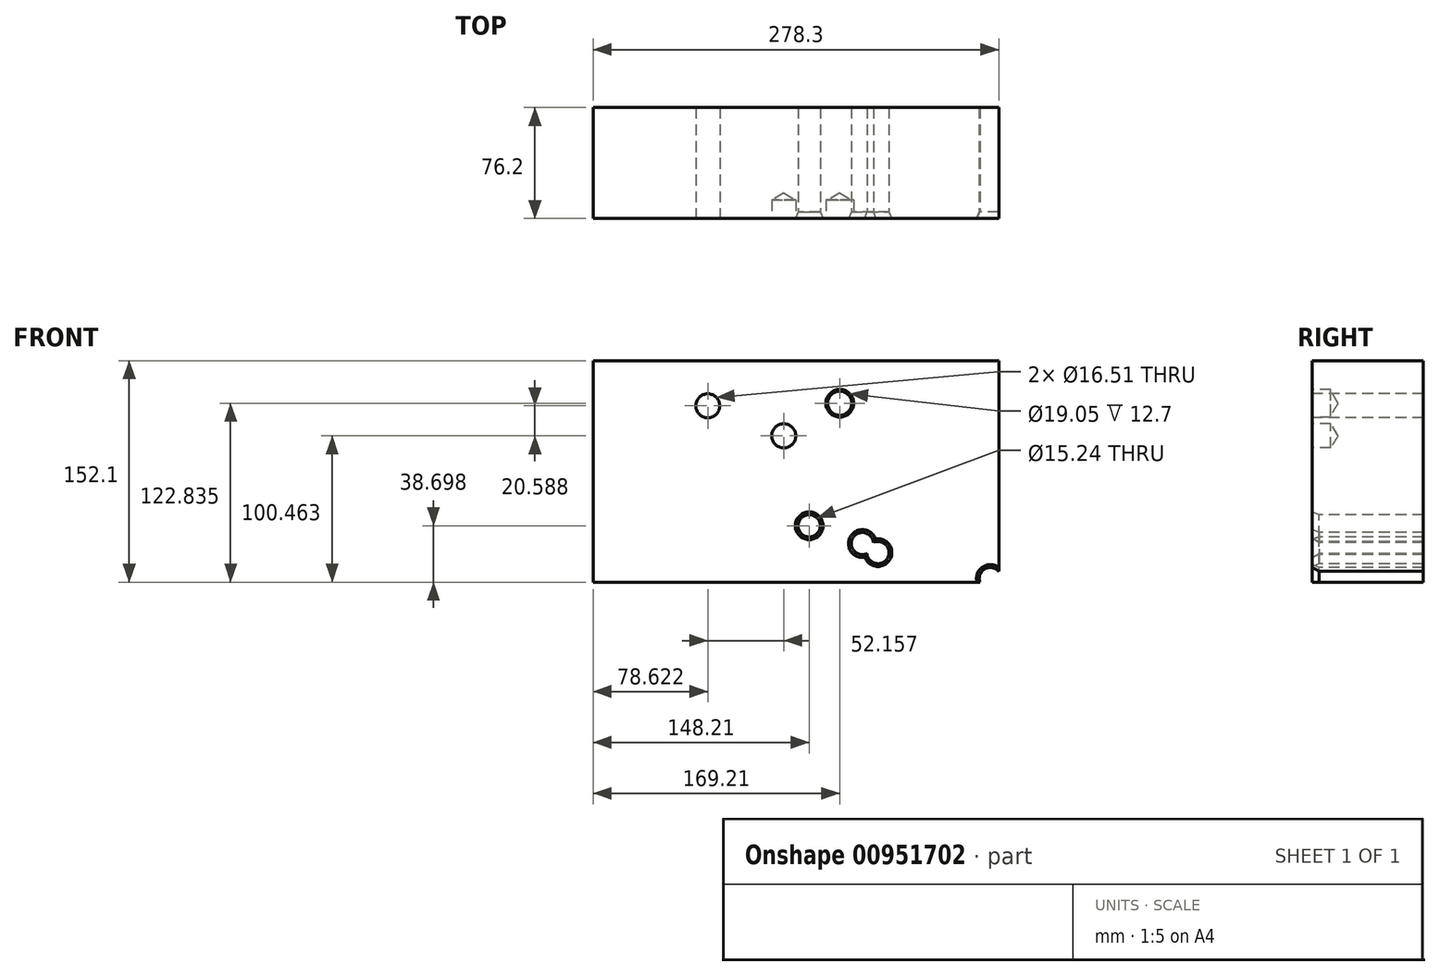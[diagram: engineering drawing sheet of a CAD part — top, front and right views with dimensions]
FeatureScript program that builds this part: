
annotation { "Feature Type Name" : "Feature", "Feature Type Description" : "" }
export const myFeature = defineFeature(function(context is Context, id is Id, definition is map)
    precondition{}
    {
        {
            var Q0;
            Q0=qCreatedBy(makeId("Front.planeOp"),FACE);
            var sketch = newSketch(context, id + "F0", { "sketchPlane" : qUnion([Q0])});
            skLineSegment(sketch, "E0.bottom", {"start": v(-137.1, 77.72) * mm, "end": v(141.2, 77.72) * mm});
            skLineSegment(sketch, "E0.top", {"start": v(-137.1, -74.38) * mm, "end": v(141.2, -74.38) * mm});
            skLineSegment(sketch, "E0.left", {"start": v(-137.1, 77.72) * mm, "end": v(-137.1, -74.38) * mm});
            skLineSegment(sketch, "E0.right", {"start": v(141.2, 77.72) * mm, "end": v(141.2, -74.38) * mm});
            skSolve(sketch);
        }
        {
            var Q0;
            Q0=makeQuery(id+"F0.imprint","IMPRINT",FACE,{"disambiguationData":[TD([[makeQuery(id+"F0.imprint","IMPRINT",EDGE,{"derivedFrom":sQuery(id+"F0.wireOp",EDGE,"E0.bottom")}),-1.0]])]});
            extrude(context, id + "F1", {"entities" : qUnion([Q0]), "depth" : 76.2 * mm, "offsetDistance" : 25.4 * mm});
        }
        {
            var Q0;
            Q0=makeQuery(id+"F1.opExtrude","CAP_FACE",FACE,{"disambiguationData":[OSD([sQuery(id+"F0.wireOp",EDGE,"E0.bottom"),sQuery(id+"F0.wireOp",EDGE,"E0.top"),sQuery(id+"F0.wireOp",EDGE,"E0.left"),sQuery(id+"F0.wireOp",EDGE,"E0.right")])],"isStart":false});
            var sketch = newSketch(context, id + "F2", { "sketchPlane" : qUnion([Q0])});
            skPoint(sketch, "E1", {"position": v(-58.49, 46.67) * mm});
            skPoint(sketch, "E2", {"position": v(-6.33, 26.08) * mm});
            skPoint(sketch, "E3", {"position": v(32.1, 48.46) * mm});
            skPoint(sketch, "E4", {"position": v(68.88, 13.87) * mm});
            skPoint(sketch, "E5", {"position": v(48.7, -4.52) * mm});
            skPoint(sketch, "E6", {"position": v(-39.14, -13.45) * mm});
            skPoint(sketch, "E7", {"position": v(-63.02, 4.4) * mm});
            skPoint(sketch, "E8", {"position": v(11.1, -35.68) * mm});
            skPoint(sketch, "E9", {"position": v(47.6, -47.9) * mm});
            skPoint(sketch, "E10", {"position": v(58.32, -54.07) * mm});
            skPoint(sketch, "E11", {"position": v(102.65, -54.07) * mm});
            skPoint(sketch, "E12", {"position": v(135.45, -71.92) * mm});
            skSolve(sketch);
        }
        {
            var Q0;
            Q0=sQuery(id+"F2.wireOp",VERTEX,"E1");
            var Q1;
            Q1=makeQuery(id+"F1.opExtrude","SWEPT_BODY",BODY,{"disambiguationData":[OSD([sQuery(id+"F0.wireOp",EDGE,"E0.bottom"),sQuery(id+"F0.wireOp",EDGE,"E0.top"),sQuery(id+"F0.wireOp",EDGE,"E0.left"),sQuery(id+"F0.wireOp",EDGE,"E0.right")])]});
            hole(context, id + "F3", {"style" : HoleStyle.SIMPLE, "endStyle" : HoleEndStyle.THROUGH, "holeDiameter" : 16.5 * mm, "majorDiameter" : 6.35 * mm, "isTappedThrough" : true, "tappedDepth" : 12.7 * mm, "tapClearance" : 3, "locations" : qUnion([Q0]), "scope" : qUnion([Q1])});
        }
        {
            var Q0;
            Q0=sQuery(id+"F2.wireOp",VERTEX,"E2");
            var Q1;
            Q1=makeQuery(id+"F1.opExtrude","SWEPT_BODY",BODY,{"disambiguationData":[OSD([sQuery(id+"F0.wireOp",EDGE,"E0.bottom"),sQuery(id+"F0.wireOp",EDGE,"E0.top"),sQuery(id+"F0.wireOp",EDGE,"E0.left"),sQuery(id+"F0.wireOp",EDGE,"E0.right")])]});
            hole(context, id + "F4", {"style" : HoleStyle.SIMPLE, "endStyle" : HoleEndStyle.BLIND, "holeDiameter" : 16.5 * mm, "majorDiameter" : 6.35 * mm, "holeDepth" : 12.7 * mm, "isTappedThrough" : true, "tappedDepth" : 12.7 * mm, "tapClearance" : 3, "locations" : qUnion([Q0]), "scope" : qUnion([Q1])});
        }
        {
            var Q0;
            Q0=sQuery(id+"F2.wireOp",VERTEX,"E3");
            var Q1;
            Q1=makeQuery(id+"F1.opExtrude","SWEPT_BODY",BODY,{"disambiguationData":[OSD([sQuery(id+"F0.wireOp",EDGE,"E0.bottom"),sQuery(id+"F0.wireOp",EDGE,"E0.top"),sQuery(id+"F0.wireOp",EDGE,"E0.left"),sQuery(id+"F0.wireOp",EDGE,"E0.right")])]});
            hole(context, id + "F5", {"style" : HoleStyle.C_BORE, "endStyle" : HoleEndStyle.BLIND, "holeDiameter" : 16.5 * mm, "cBoreDiameter" : 19.05 * mm, "cBoreDepth" : 12.7 * mm, "majorDiameter" : 6.35 * mm, "holeDepth" : 12.7 * mm, "isTappedThrough" : true, "tappedDepth" : 12.7 * mm, "tapClearance" : 3, "locations" : qUnion([Q0]), "scope" : qUnion([Q1])});
        }
        {
            var Q0;
            Q0=sQuery(id+"F2.wireOp",VERTEX,"E8");
            var Q1;
            Q1=makeQuery(id+"F1.opExtrude","SWEPT_BODY",BODY,{"disambiguationData":[OSD([sQuery(id+"F0.wireOp",EDGE,"E0.bottom"),sQuery(id+"F0.wireOp",EDGE,"E0.top"),sQuery(id+"F0.wireOp",EDGE,"E0.left"),sQuery(id+"F0.wireOp",EDGE,"E0.right")])]});
            hole(context, id + "F6", {"style" : HoleStyle.C_SINK, "endStyle" : HoleEndStyle.THROUGH, "holeDiameter" : 15.24 * mm, "cSinkDiameter" : 19.05 * mm, "cSinkAngle" : 45 * degree, "majorDiameter" : 6.35 * mm, "isTappedThrough" : true, "tappedDepth" : 12.7 * mm, "tapClearance" : 3, "locations" : qUnion([Q0]), "scope" : qUnion([Q1])});
        }
        {
            var Q0;
            Q0=sQuery(id+"F2.wireOp",VERTEX,"E12");
            var Q1;
            Q1=sQuery(id+"F2.wireOp",VERTEX,"E9");
            var Q2;
            Q2=sQuery(id+"F2.wireOp",VERTEX,"E10");
            var Q3;
            Q3=makeQuery(id+"F1.opExtrude","SWEPT_BODY",BODY,{"disambiguationData":[OSD([sQuery(id+"F0.wireOp",EDGE,"E0.bottom"),sQuery(id+"F0.wireOp",EDGE,"E0.top"),sQuery(id+"F0.wireOp",EDGE,"E0.left"),sQuery(id+"F0.wireOp",EDGE,"E0.right")])]});
            hole(context, id + "F7", {"style" : HoleStyle.C_SINK, "endStyle" : HoleEndStyle.THROUGH, "holeDiameter" : 15.24 * mm, "cSinkDiameter" : 19.05 * mm, "cSinkAngle" : 45 * degree, "majorDiameter" : 6.35 * mm, "isTappedThrough" : true, "tappedDepth" : 12.7 * mm, "tapClearance" : 3, "locations" : qUnion([Q0, Q1, Q2]), "scope" : qUnion([Q3])});
        }
    });
